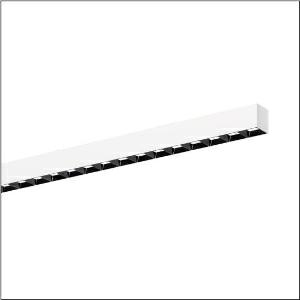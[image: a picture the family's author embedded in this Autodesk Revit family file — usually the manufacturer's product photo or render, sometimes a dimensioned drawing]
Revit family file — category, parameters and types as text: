
# Revit family: silica_r__21_51mx24da34wb_1271
name_source: partatom
category: Lighting Fixtures
units: mm (PartAtom-declared; Revit-internal decimal feet)

## family parameters
Cut with Voids When Loaded = No
Host = Face
Light Source = No
Part Type = Normal
Room Calculation Point = No
Round Connector Dimension = Use Diameter
Shared = No

## types (1)
- --- (1 x LED, 4320 lm, 32.1 W, 3000K)
    Apparent Load = 32 VA
    CIE Flux Codes = 74 94 99 100 100
    Color Rendering = 80
    Color Temperature = 3000K
    Default Elevation = 1800 mm
    Description = Silica® 21, office luminaire, primary light control with darklight reflector, of PMMA, black, CAT 2 (L<= 3000cd/m²), light emission: direct distribution, primary light characteristic: asymmetric, installation type: surface-mounted, LED, rated luminous flux: 4.320lm, luminous efficacy: 135lm/W, light colour: 830, colour temperature: 3000K, with terminal, 3+2-pole, max. 2.5mm², mains connection: 220..240V, AC, 50/60Hz, rated input power: 32.1W, luminaire housing, of aluminium, traffic white (RAL 9016), length: 1.204mm, width: 53mm, height: 53mm, protection rating (complete): IP20, insulation class (complete): insulation class I (protective earthing), certification: CE, permissible operating ambient temperature: 0..+35°C, standard: EN 50419, packaging unit: 1 piece
    Height = 0 mm  [stored 0 ft]
    Lamp = 1 x LED
    Lamp Light Flux = 4320 lm
    Lamp Power = 32.1 W
    Lamp count = 1
    Length = 1204 mm
    Luminous efficacy = 135 lm/W
    Manufacturer = Siteco
    ModVariant = No
    Model = 51MX24DA34WB
    Mounting Place = Ceiling
    Mounting Type = Recessed
    Number of Poles = 1
    OnlyDefault = Yes
    Power Factor = 1
    Product Name = Silica® 21
    Product group = office luminaire | ceiling recessed
    ProductGroupID = 400
    Protection Class = Protection class I
    Protection Degree = IP 20
    RLX_Detail_Level = 1
    RLX_Emergency_Light_Flux = 0 lm
    RLX_Emergency_Type = 0
    RLX_Emergency_Type_DB = No
    RlxData = <blob elided: 41641 chars, md5=d9cf7147>
    Socket = socket
    Standby Power = 0 W
    System Light Flux = 4320 lm
    System Power = 32 W
    Type Comments = factory setting: luminous flux: 100 % | dim-lin: 254 | 448 mA
    Type Image = l_1335873.jpg
    URL = http://relux.com
    VarID = @adj_092747
    Voltage = 0 V
    Weight = 0.00 kg
    Width = 53 mm

note: [stored X ft] marks values corroborated as IEEE doubles in the binary element streams (Revit-internal decimal feet)

## geometry (parser evidence)
native form markers: Blend x4, Sweep x9
no freeform markers — native parametric forms only
